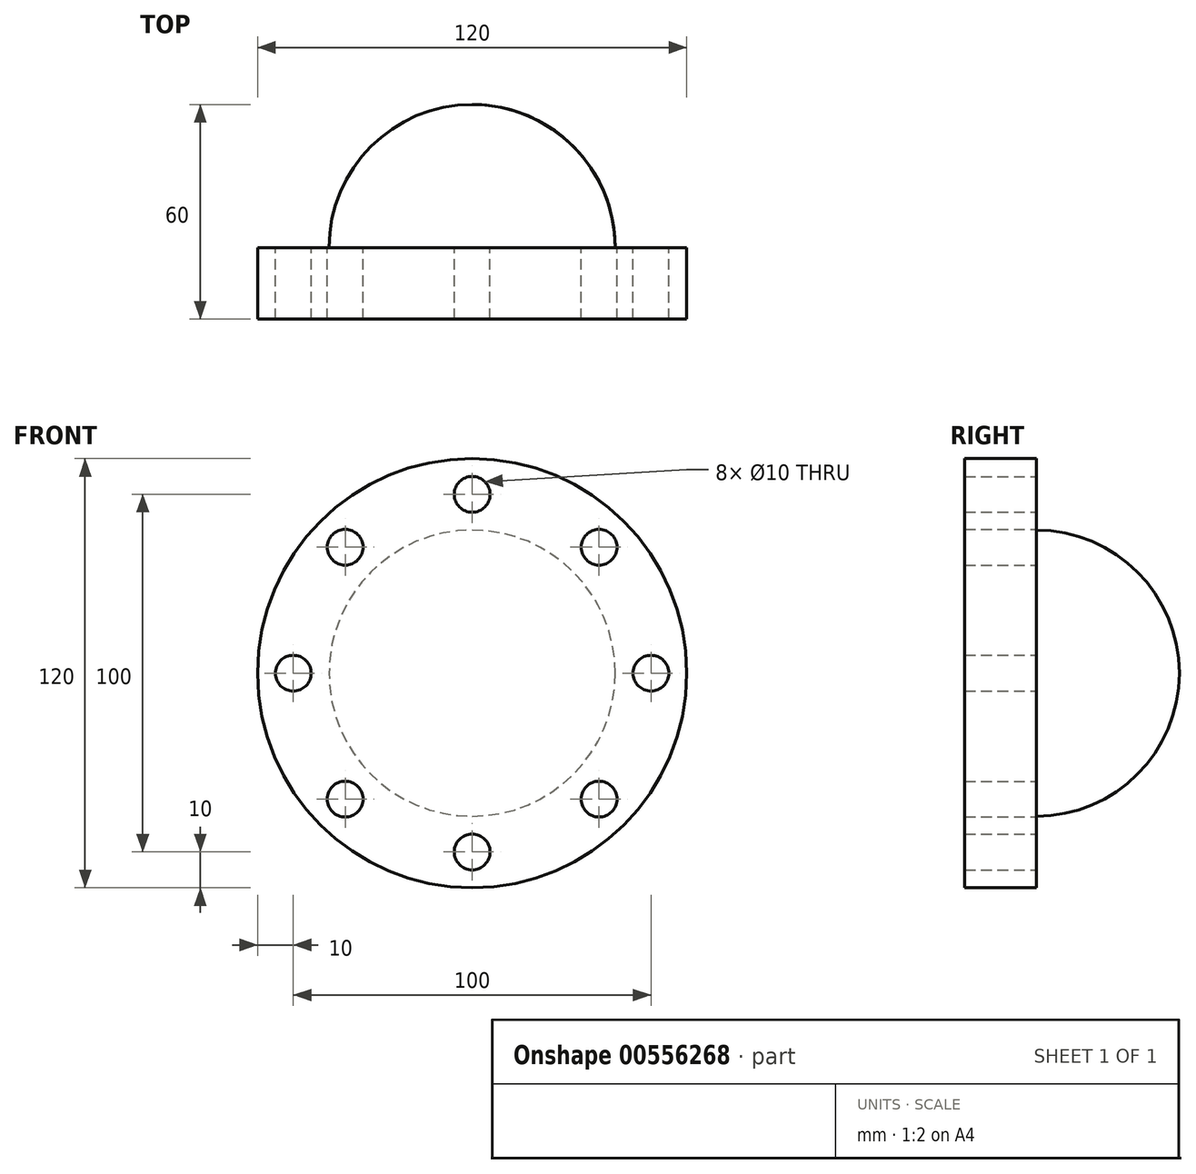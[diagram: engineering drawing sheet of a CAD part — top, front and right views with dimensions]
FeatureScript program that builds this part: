
annotation { "Feature Type Name" : "Feature", "Feature Type Description" : "" }
export const myFeature = defineFeature(function(context is Context, id is Id, definition is map)
    precondition{}
    {
        {
            var Q0;
            Q0=qCreatedBy(makeId("Front.planeOp"),FACE);
            var sketch = newSketch(context, id + "F0", { "sketchPlane" : qUnion([Q0])});
            skCircle(sketch, "E0", {"center": v(0, 0) * mm, "radius": 60 * mm});
            skCircle(sketch, "E1", {"center": v(0, 0) * mm, "radius": 50 * mm, "construction": true});
            skPoint(sketch, "E2", {"position": v(0, 50) * mm});
            skPoint(sketch, "E3", {"position": v(-50, 0) * mm});
            skPoint(sketch, "E4", {"position": v(0, -50) * mm});
            skPoint(sketch, "E5", {"position": v(50, 0) * mm});
            skPoint(sketch, "E6", {"position": v(-35.5, 35.22) * mm});
            skPoint(sketch, "E7.MirrorP", {"position": v(35.5, 35.22) * mm});
            skPoint(sketch, "E8.MirrorP", {"position": v(-35.5, -35.22) * mm});
            skPoint(sketch, "E9.MirrorP", {"position": v(35.5, -35.22) * mm});
            skCircle(sketch, "E10", {"center": v(0, 50) * mm, "radius": 5 * mm});
            skCircle(sketch, "E11", {"center": v(35.5, 35.22) * mm, "radius": 5 * mm});
            skCircle(sketch, "E12", {"center": v(50, 0) * mm, "radius": 5 * mm});
            skCircle(sketch, "E13", {"center": v(35.5, -35.22) * mm, "radius": 5 * mm});
            skCircle(sketch, "E14", {"center": v(0, -50) * mm, "radius": 5 * mm});
            skCircle(sketch, "E15", {"center": v(-35.5, -35.22) * mm, "radius": 5 * mm});
            skCircle(sketch, "E16", {"center": v(-50, 0) * mm, "radius": 5 * mm});
            skCircle(sketch, "E17", {"center": v(-35.5, 35.22) * mm, "radius": 5 * mm});
            skSolve(sketch);
        }
        {
            var Q0;
            Q0 = qSketchRegion(id + "F0", true);
            extrude(context, id + "F1", {"entities" : qUnion([Q0]), "depth" : 20 * mm, "offsetDistance" : 25 * mm});
        }
        {
            var Q0;
            Q0=qCreatedBy(makeId("Top.planeOp"),FACE);
            var sketch = newSketch(context, id + "F2", { "sketchPlane" : qUnion([Q0])});
            skLineSegment(sketch, "E18.0", {"start": v(60, 0) * mm, "end": v(-60, 0) * mm});
            skArc(sketch, "E19", {"start": v(40, 0) * mm, "mid": v(28.28, 28.28) * mm, "end": v(0, 40) * mm});
            skLineSegment(sketch, "E20", {"start": v(0, 0) * mm, "end": v(0, 40) * mm});
            skSolve(sketch);
        }
        {
            var Q0;
            Q0 = qSketchRegion(id + "F2", true);
            var Q1;
            Q1=sQuery(id+"F2.wireOp",EDGE,"E20");
            revolve(context, id + "F3", {"operationType" : NewBodyOperationType.ADD, "entities" : qUnion([Q0]), "axis" : qUnion([Q1]), "revolveType" : RevolveType.FULL});
        }
    });
